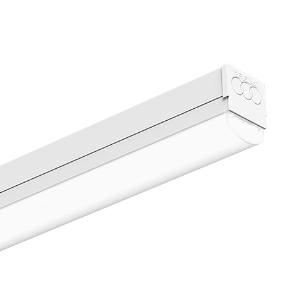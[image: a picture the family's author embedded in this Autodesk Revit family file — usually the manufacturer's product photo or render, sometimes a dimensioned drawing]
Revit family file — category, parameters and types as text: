
# Revit family: 3f_filippi_-_3f_zeta_d_3f_filippi_-_10873_-_3f_zeta_d_2x22_led_l1489
name_source: partatom
category: Lighting Fixtures
units: mm (PartAtom-declared; Revit-internal decimal feet)

## family parameters
Cut with Voids When Loaded = No
Host = Face
Light Source = No
Part Type = Normal
Room Calculation Point = No
Round Connector Dimension = Use Diameter
Shared = No

## types (1)
- 3F Filippi - 3F Zeta D (1 x LED, 6236 lm, 49 W, 4000 K)
    Apparent Load = 49 VA
    Approval mark = CE
    CIE Flux Codes = 42 71 90 91 100
    Color Rendering = 80
    Color Temperature = 4000 K
    Control Gear = Electronic ballast
    Default Elevation = 1800 mm
    Description = ILLUMINOTECHNICAL
Luminous efficiency 100% (DLOR 91%, ULOR 9%).
Initial luminous flux of the luminaire 6236 lm.
Diffused symmetric distribution.
Installation Interdistance Transv.D = 1.31 x hu - Long.D = 1.25 x hu.
Tabular UGR (CIE 117 - 4H-8H; S=0.25H; 70/50/20): RUG 26.2 - 24.6.
Beam angle: 130° - 112°.
Luminous efficacy 127 lm/W.
Lifetime (L93/B10): 30000 h. (tq+25°C)
Lifetime (L90/B10): 50000 h. (tq+25°C)
Lifetime (L85/B10): 80000 h. (tq+25°C)
Lifetime (L80/B10): 100000 h. (tq+25°C)
Sudden decreased luminous flux after 50000 hours: 0% (C0).
Photobiological safety in compliance with IEC/TR 62778: RG0 risk exempt, (IEC 62471).
In compliance with IEC/EN 62722-2-1 - IEC/EN 62717 standards.

SOURCE
2 linear LED modules 22W/840.
Energy efficiency class (UE 2019/2020 - UE 2019/2015): D.
CIE 13.3 Colour rendering index: CRI >80 (R9 <50%).
IES TM-30 Fidelity Index: Rf = 84 Rg = 95.
CCT nominal colour temperature 4000 K.
Colour initial tolerance (MacAdam): SDCM 3.

MECHANICAL
Housing in hot-galvanised steel, painted in white polyester, obtained through rolling process.
Light unit in hot-galvanised steel, painted in white polyester base with fixing springs and retractable safety hooks in stainless steel.
Curved screen in self-extinguishing polycarbonate, UV stabilised, opal, with smooth outer surface.
End caps in white polycarbonate.
Pair of stainless steel sliding brackets with sliding block screws.
Luminaire with limited surface temperature. - D - (EN 60598-2-24)
Dimensions: 1489x62 mm, height 81 mm. Weight 3.485 kg.
IP40 protection degree.
Mechanical strength to impacts IK06 (1 joule).
Glow-wire test resistance 850°C.

ELECTRICAL
Halogen Free electronic wiring 230V-50/60Hz, power factor 0.95, THD <25%, constant output current, SELV, class I, 1 driver.
Power of the luminaire 49 W.
ENEC - CE.
SAFE FLICKER: PstLM=<1 and SVM=<0.4 (IEC TR 61547-1 and IEC TR 63158), to ensure a more comfortable and safe light.
Luminaire compliant with EN 60598-2-22 for power supply from a centralised emergency system CPSS (Central Power Supply System), not incorporated in the luminaire - high risk areas excluded. The default power and flux are 100% in AC and 100% in DC.
Ambient temperature from 0°C to +25°C.
Temperature class T6 max 85°C.
Relative humidity UR: <85%.

INSTALLATION
Ceiling / Suspended / Wall.
All accessories dedicated to this product are available on the Catalog and on our website www.3F-Filippi.com.

APPLICATIONS
Suitable product for food production plants (HACCP), IFS (Food Version 6), BRC (GSFS Food Version 7).
In commercial environments, exhibition areas, shops and stores.

WARNING
Luminaire designed for disposal/recycling at end-of-life.
Replaceable (LED only) light source by a professional. Replaceable control gear by a professional.
    Height = 81 mm
    Lamp = 1 x LED
    Lamp Light Flux = 6236 lm
    Lamp Power = 49 W
    Lamp count = 1
    Length = 1489 mm
    Lifetime = 50000 h
    Luminous efficacy = 127 lm/W
    Manufacturer = 3F Filippi
    ModVariant = No
    Model = 3F Filippi - 10873 - 3F Zeta D 2x22 LED L1489
    Mounting Place = Ceiling
    Mounting Type = Pendant
    Number of Poles = 1
    OnlyDefault = Yes
    Power Factor = 1
    Product Name = 3F Filippi - 3F Zeta D
    Product group = pendant luminaire
    ProductGroupID = 9
    Protection Class = Protection class I
    Protection Degree = IP 40
    RLX_Detail_Level = 1
    RLX_Emergency_Light_Flux = 0 lm
    RLX_Emergency_Type = 0
    RLX_Emergency_Type_DB = No
    RlxData = <blob elided: 33321 chars, md5=5c356807>
    Socket = socket
    Standby Power = 0 W
    System Light Flux = 6236 lm
    System Power = 49 W
    Type Comments = Product without accessories
    Type Image = 3ffilippi_3f_zeta_d.jpg
    URL = http://relux.com
    VarID = ---
    Voltage = 0 V
    Weight = 0.00 kg
    Width = 62 mm  [stored 0.203412 ft]

note: [stored X ft] marks values corroborated as IEEE doubles in the binary element streams (Revit-internal decimal feet)

## geometry (parser evidence)
native form markers: Blend x4, Sweep x13
no freeform markers — native parametric forms only
